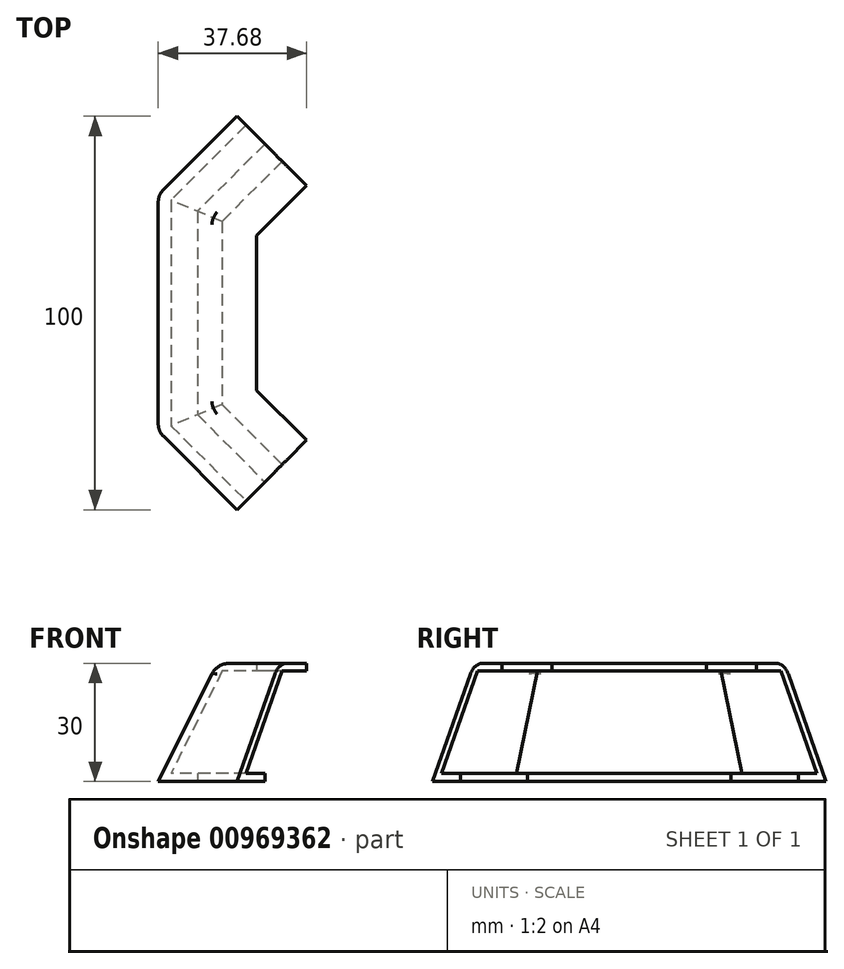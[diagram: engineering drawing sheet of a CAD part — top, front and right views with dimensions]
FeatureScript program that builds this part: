
annotation { "Feature Type Name" : "Feature", "Feature Type Description" : "" }
export const myFeature = defineFeature(function(context is Context, id is Id, definition is map)
    precondition{}
    {
        {
            var Q0;
            Q0=qCreatedBy(makeId("Top.planeOp"),FACE);
            var sketch = newSketch(context, id + "F0", { "sketchPlane" : qUnion([Q0])});
            skLineSegment(sketch, "E0", {"start": v(-20, 30) * mm, "end": v(-20, -30) * mm});
            skLineSegment(sketch, "E1", {"start": v(-20, -30) * mm, "end": v(0, -50) * mm});
            skLineSegment(sketch, "E2", {"start": v(-20, 30) * mm, "end": v(0, 50) * mm});
            skSolve(sketch);
        }
        {
            var Q0;
            Q0=qCreatedBy(makeId("Front.planeOp"),FACE);
            var sketch = newSketch(context, id + "F1", { "sketchPlane" : qUnion([Q0])});
            skLineSegment(sketch, "E3", {"start": v(-10, 0) * mm, "end": v(-20, 0) * mm});
            skLineSegment(sketch, "E4", {"start": v(-20, 0) * mm, "end": v(-5, 30) * mm});
            skLineSegment(sketch, "E5", {"start": v(-5, 30) * mm, "end": v(5, 30) * mm});
            skLineSegment(sketch, "E6", {"start": v(5, 30) * mm, "end": v(5, 28) * mm});
            skLineSegment(sketch, "E7", {"start": v(5, 28) * mm, "end": v(-3.76, 28) * mm});
            skLineSegment(sketch, "E8", {"start": v(-3.76, 28) * mm, "end": v(-16.76, 2) * mm});
            skLineSegment(sketch, "E9", {"start": v(-16.76, 2) * mm, "end": v(-10, 2) * mm});
            skLineSegment(sketch, "E10", {"start": v(-10, 2) * mm, "end": v(-10, 0) * mm});
            skSolve(sketch);
        }
        {
            var Q0;
            Q0=makeQuery(id+"F1.imprint","IMPRINT",FACE,{"disambiguationData":[TD([[makeQuery(id+"F1.imprint","IMPRINT",EDGE,{"derivedFrom":sQuery(id+"F1.wireOp",EDGE,"E3")}),-1.0]])]});
            var Q1;
            Q1=sQuery(id+"F0.wireOp",EDGE,"E1");
            var Q2;
            Q2=sQuery(id+"F0.wireOp",EDGE,"E2");
            var Q3;
            Q3=sQuery(id+"F0.wireOp",EDGE,"E0");
            sweep(context, id + "F2", {"profiles" : qUnion([Q0]), "path" : qUnion([Q1, Q2, Q3])});
        }
        {
            var Q0;
            Q0=makeQuery(id+"F2.opSweep","SWEPT_EDGE",EDGE,{"disambiguationData":[OSD([sQuery(id+"F0.wireOp",EDGE,"E0"),sQuery(id+"F1.wireOp",EDGE,"E4"),sQuery(id+"F1.wireOp",EDGE,"E5")])]});
            var Q1;
            Q1=makeQuery(id+"F2.opSweep","SWEPT_EDGE",EDGE,{"disambiguationData":[OSD([sQuery(id+"F0.wireOp",EDGE,"E2"),sQuery(id+"F1.wireOp",EDGE,"E4"),sQuery(id+"F1.wireOp",EDGE,"E5")])]});
            var Q2;
            Q2=makeQuery(id+"F2.opSweep","SWEPT_EDGE",EDGE,{"disambiguationData":[OSD([sQuery(id+"F0.wireOp",EDGE,"E1"),sQuery(id+"F1.wireOp",EDGE,"E4"),sQuery(id+"F1.wireOp",EDGE,"E5")])]});
            var Q3;
            Q3=makeQuery(id+"F2.opSweep","MID_CAP_EDGE",EDGE,{"disambiguationData":[OSD([sQuery(id+"F0.wireOp",VERTEX,"E0.end"),sQuery(id+"F1.wireOp",EDGE,"E4")])],"capPos":2.0});
            var Q4;
            Q4=makeQuery(id+"F2.opSweep","MID_CAP_EDGE",EDGE,{"disambiguationData":[OSD([sQuery(id+"F0.wireOp",VERTEX,"E0.start"),sQuery(id+"F1.wireOp",EDGE,"E4")])],"capPos":1.0});
            fillet(context, id + "F3", {"entities" : qUnion([Q0, Q1, Q2, Q3, Q4]), "radius" : 5 * mm, "tangentPropagation" : true, "allowEdgeOverflow" : false});
        }
    });
